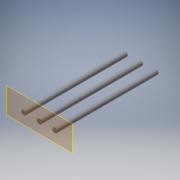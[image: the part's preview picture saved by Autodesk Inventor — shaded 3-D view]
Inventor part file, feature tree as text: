
AUTODESK INVENTOR PART (.ipt)
format: ipt  version: 2016 (Build 200138000, 138)  size: 93,184 bytes
history: native  units: in
note: dims shown in document units (in); Inventor stores cm internally (conversion verified against a paired STEP export)
features: reference x3, plane x1, extrude x1, sketch x1
ambient origin geometry x8: Origin, YZ Plane, XZ Plane, XY Plane, X Axis, Y Axis, Z Axis, Center Point
bodies: Solid1 (feature_tree)
feature tree (6):
  plane  "Work Plane1"
  extrude  "Extrusion1"  [1 undecoded]
  sketch  "Sketch1"  dims[d0=6.5625in d1=0.0in]
  reference  "Reference1"
  reference  "Reference2"
  reference  "Reference3"
note: 1 required parameter value undecoded (feature->parameter linkage not recoverable at this tier; creation-order binding heuristic only, values carry confidence <= 0.55)
